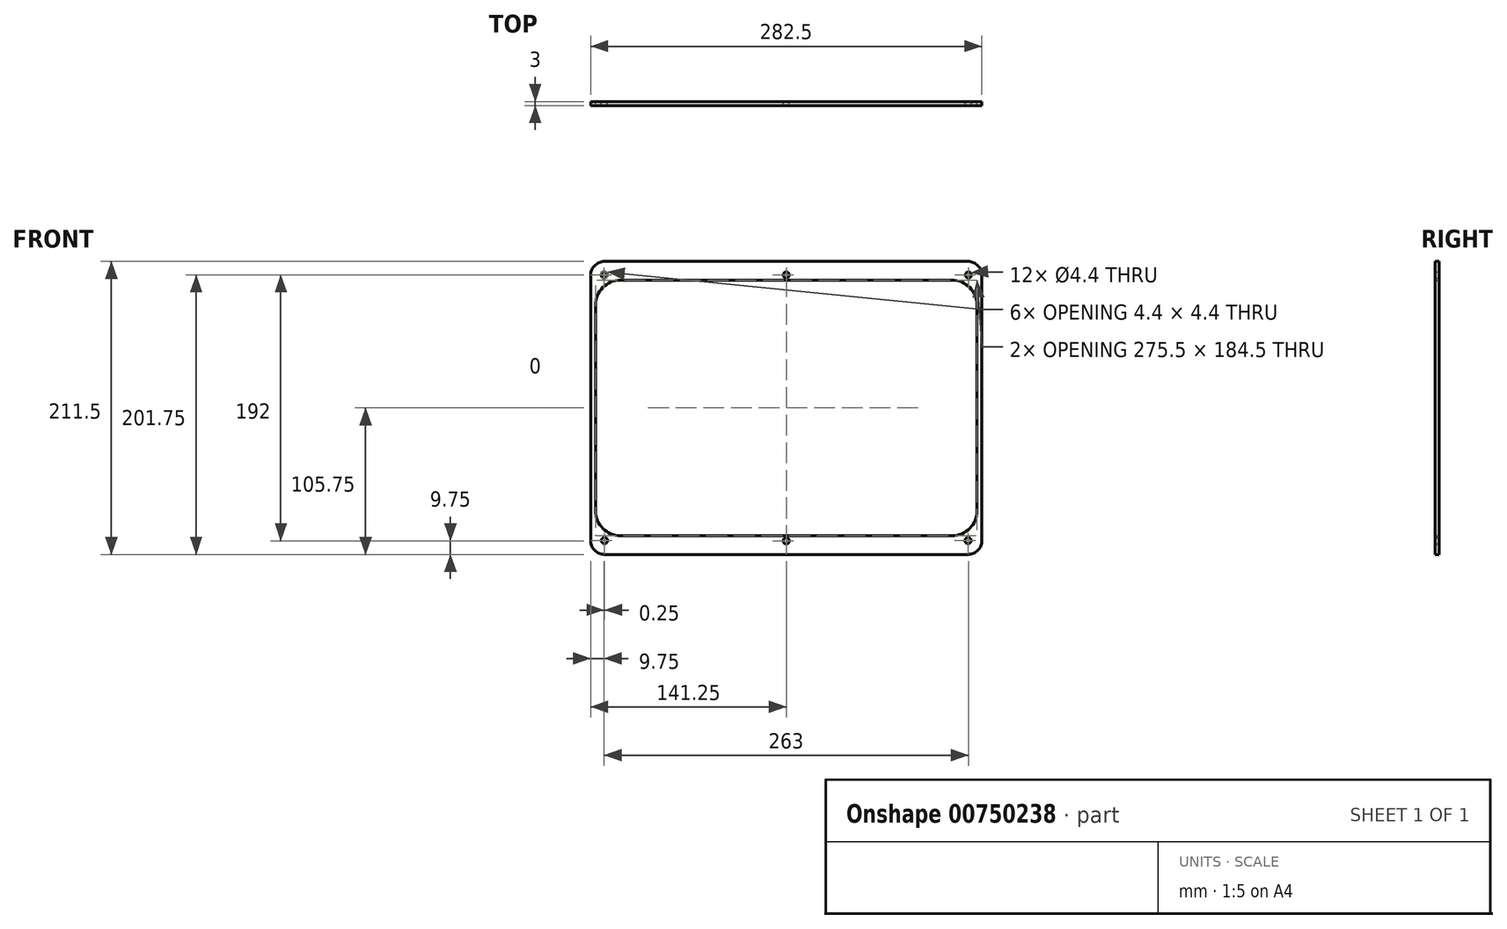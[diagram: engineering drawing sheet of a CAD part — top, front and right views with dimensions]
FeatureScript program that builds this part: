
annotation { "Feature Type Name" : "Feature", "Feature Type Description" : "" }
export const myFeature = defineFeature(function(context is Context, id is Id, definition is map)
    precondition{}
    {
        {
            var Q0;
            Q0=qCreatedBy(makeId("Front.planeOp"),FACE);
            var sketch = newSketch(context, id + "F0", { "sketchPlane" : qUnion([Q0])});
            skLineSegment(sketch, "E0.bottom", {"start": v(131.25, -105.75) * mm, "end": v(-131.25, -105.75) * mm});
            skLineSegment(sketch, "E0.top", {"start": v(131.25, 105.75) * mm, "end": v(-131.25, 105.75) * mm});
            skLineSegment(sketch, "E0.left", {"start": v(141.25, -95.75) * mm, "end": v(141.25, 95.75) * mm});
            skLineSegment(sketch, "E0.right", {"start": v(-141.25, -95.75) * mm, "end": v(-141.25, 95.75) * mm});
            skPoint(sketch, "E0.middle", {"position": v(0, 0) * mm});
            skLineSegment(sketch, "E1.bottom", {"start": v(119.75, -92.25) * mm, "end": v(-119.75, -92.25) * mm});
            skLineSegment(sketch, "E1.top", {"start": v(119.75, 92.25) * mm, "end": v(-119.75, 92.25) * mm});
            skLineSegment(sketch, "E1.left", {"start": v(137.75, -74.25) * mm, "end": v(137.75, 74.25) * mm});
            skLineSegment(sketch, "E1.right", {"start": v(-137.75, -74.25) * mm, "end": v(-137.75, 74.25) * mm});
            skPoint(sketch, "E2.visualSharp", {"position": v(-137.75, 92.25) * mm});
            skArc(sketch, "E2.filletArc", {"start": v(-119.75, 92.25) * mm, "mid": v(-132.48, 86.98) * mm, "end": v(-137.75, 74.25) * mm});
            skPoint(sketch, "E3.visualSharp", {"position": v(137.75, 92.25) * mm});
            skArc(sketch, "E3.filletArc", {"start": v(137.75, 74.25) * mm, "mid": v(132.48, 86.98) * mm, "end": v(119.75, 92.25) * mm});
            skPoint(sketch, "E4.visualSharp", {"position": v(137.75, -92.25) * mm});
            skArc(sketch, "E4.filletArc", {"start": v(119.75, -92.25) * mm, "mid": v(132.48, -86.98) * mm, "end": v(137.75, -74.25) * mm});
            skPoint(sketch, "E5.visualSharp", {"position": v(-137.75, -92.25) * mm});
            skArc(sketch, "E5.filletArc", {"start": v(-137.75, -74.25) * mm, "mid": v(-132.48, -86.98) * mm, "end": v(-119.75, -92.25) * mm});
            skPoint(sketch, "E6.visualSharp", {"position": v(-141.25, 105.75) * mm});
            skArc(sketch, "E6.filletArc", {"start": v(-131.25, 105.75) * mm, "mid": v(-138.32, 102.82) * mm, "end": v(-141.25, 95.75) * mm});
            skPoint(sketch, "E7.visualSharp", {"position": v(141.25, 105.75) * mm});
            skArc(sketch, "E7.filletArc", {"start": v(141.25, 95.75) * mm, "mid": v(138.32, 102.82) * mm, "end": v(131.25, 105.75) * mm});
            skPoint(sketch, "E8.visualSharp", {"position": v(141.25, -105.75) * mm});
            skArc(sketch, "E8.filletArc", {"start": v(131.25, -105.75) * mm, "mid": v(138.32, -102.82) * mm, "end": v(141.25, -95.75) * mm});
            skPoint(sketch, "E9.visualSharp", {"position": v(-141.25, -105.75) * mm});
            skArc(sketch, "E9.filletArc", {"start": v(-141.25, -95.75) * mm, "mid": v(-138.32, -102.82) * mm, "end": v(-131.25, -105.75) * mm});
            skLineSegment(sketch, "E10.bottom", {"start": v(131.5, -96) * mm, "end": v(-131.5, -96) * mm, "construction": true});
            skLineSegment(sketch, "E10.top", {"start": v(131.5, 96) * mm, "end": v(-131.5, 96) * mm, "construction": true});
            skLineSegment(sketch, "E10.left", {"start": v(131.5, -96) * mm, "end": v(131.5, 96) * mm, "construction": true});
            skLineSegment(sketch, "E10.right", {"start": v(-131.5, -96) * mm, "end": v(-131.5, 96) * mm, "construction": true});
            skPoint(sketch, "E11", {"position": v(0, 96) * mm});
            skPoint(sketch, "E12", {"position": v(0, -96) * mm});
            skSolve(sketch);
        }
        {
            var Q0;
            Q0=makeQuery(id+"F0.imprint","IMPRINT",FACE,{"disambiguationData":[TD([[makeQuery(id+"F0.imprint","IMPRINT",EDGE,{"derivedFrom":sQuery(id+"F0.wireOp",EDGE,"E0.bottom")}),-1.0]])]});
            extrude(context, id + "F1", {"entities" : qUnion([Q0]), "depth" : 3 * mm, "offsetDistance" : 25 * mm});
        }
        {
            var Q0;
            Q0=sQuery(id+"F0.wireOp",VERTEX,"E10.right.end");
            var Q1;
            Q1=sQuery(id+"F0.wireOp",VERTEX,"E11");
            var Q2;
            Q2=sQuery(id+"F0.wireOp",VERTEX,"E10.top.start");
            var Q3;
            Q3=sQuery(id+"F0.wireOp",VERTEX,"E8.filletArc.center");
            var Q4;
            Q4=sQuery(id+"F0.wireOp",VERTEX,"E12");
            var Q5;
            Q5=sQuery(id+"F0.wireOp",VERTEX,"E9.filletArc.center");
            var Q6;
            Q6=makeQuery(id+"F1.opExtrude","SWEPT_BODY",BODY,{"disambiguationData":[OSD([sQuery(id+"F0.wireOp",EDGE,"E0.bottom"),sQuery(id+"F0.wireOp",EDGE,"E0.top"),sQuery(id+"F0.wireOp",EDGE,"E0.left"),sQuery(id+"F0.wireOp",EDGE,"E0.right"),sQuery(id+"F0.wireOp",EDGE,"E1.bottom"),sQuery(id+"F0.wireOp",EDGE,"E1.top"),sQuery(id+"F0.wireOp",EDGE,"E1.left"),sQuery(id+"F0.wireOp",EDGE,"E1.right"),sQuery(id+"F0.wireOp",EDGE,"E2.filletArc"),sQuery(id+"F0.wireOp",EDGE,"E3.filletArc"),sQuery(id+"F0.wireOp",EDGE,"E4.filletArc"),sQuery(id+"F0.wireOp",EDGE,"E5.filletArc"),sQuery(id+"F0.wireOp",EDGE,"E6.filletArc"),sQuery(id+"F0.wireOp",EDGE,"E7.filletArc"),sQuery(id+"F0.wireOp",EDGE,"E8.filletArc"),sQuery(id+"F0.wireOp",EDGE,"E9.filletArc")])]});
            hole(context, id + "F2", {"style" : HoleStyle.SIMPLE, "endStyle" : HoleEndStyle.THROUGH, "oppositeDirection" : true, "standardTappedOrClearance" : lookupTablePath({ "standard" : "ISO", "fit" : "Normal", "size" : "M4", "type" : "Clearance" }), "standardBlindInLast" : lookupTablePath({ "fit" : "Standard", "standard" : "ISO", "size" : "M4", "type" : "Clearance" }), "holeDiameter" : 4.4 * mm, "majorDiameter" : 6 * mm, "isTappedThrough" : true, "tappedDepth" : 12 * mm, "tapClearance" : 3, "locations" : qUnion([Q0, Q1, Q2, Q3, Q4, Q5]), "scope" : qUnion([Q6])});
        }
    });
